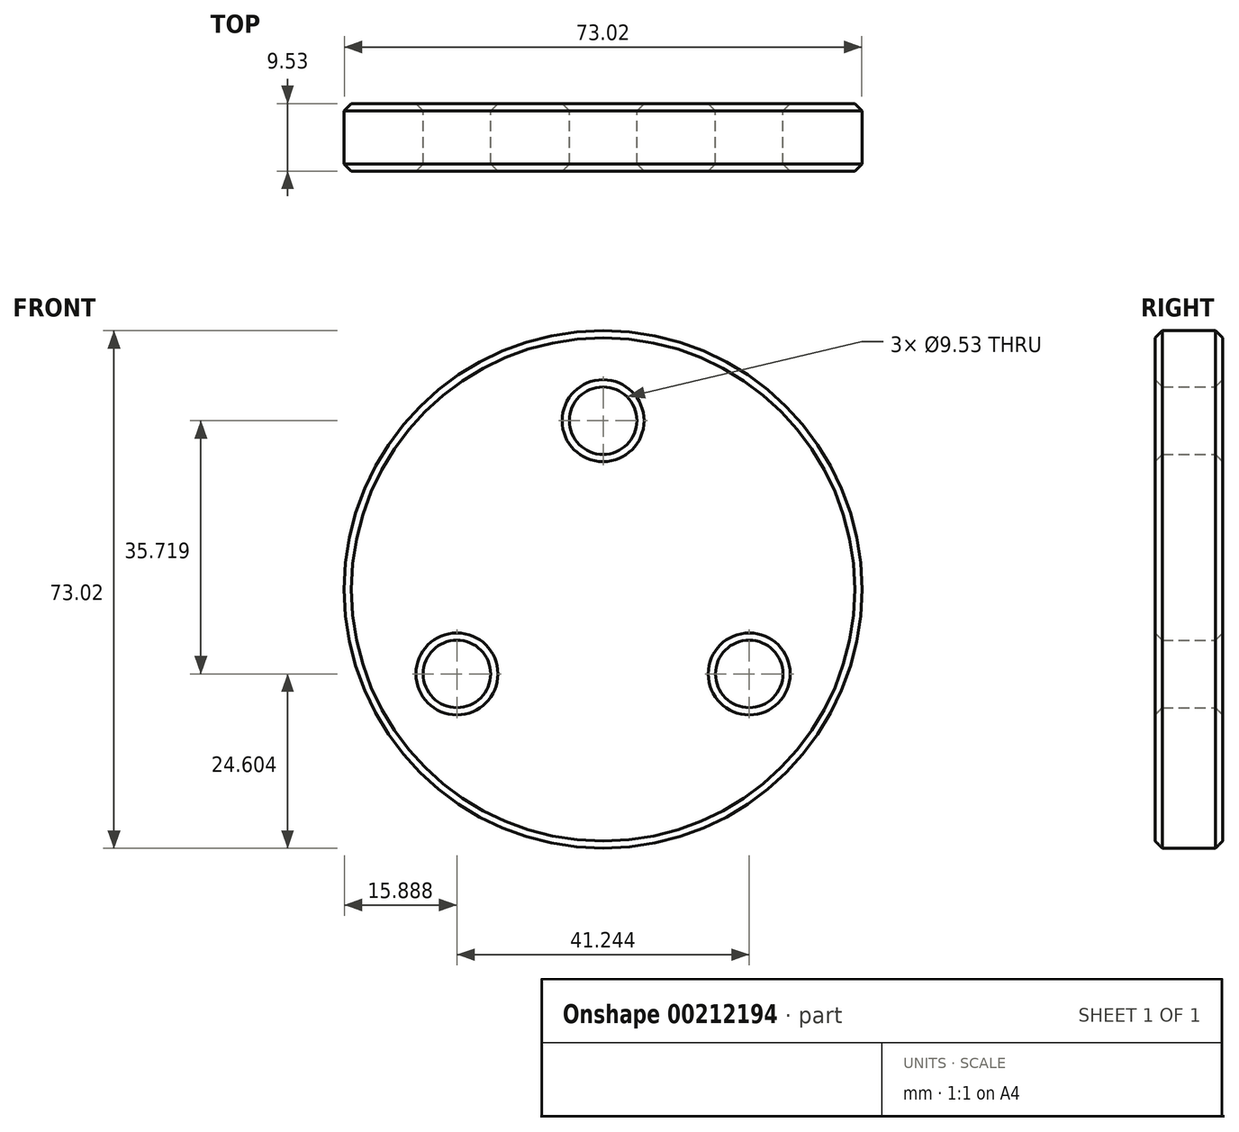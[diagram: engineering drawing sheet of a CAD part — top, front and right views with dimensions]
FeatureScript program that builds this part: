
annotation { "Feature Type Name" : "Feature", "Feature Type Description" : "" }
export const myFeature = defineFeature(function(context is Context, id is Id, definition is map)
    precondition{}
    {
        {
            var Q0;
            Q0=qCreatedBy(makeId("Front.planeOp"),FACE);
            var sketch = newSketch(context, id + "F0", { "sketchPlane" : qUnion([Q0])});
            skCircle(sketch, "E0", {"center": v(0, 0) * mm, "radius": 36.51 * mm});
            skCircle(sketch, "E1", {"center": v(0, 0) * mm, "radius": 23.81 * mm, "construction": true});
            skCircle(sketch, "E2", {"center": v(0, 23.81) * mm, "radius": 4.76 * mm});
            skCircle(sketch, "E3.1.0", {"center": v(-20.62, -11.9) * mm, "radius": 4.76 * mm});
            skCircle(sketch, "E3.2.0", {"center": v(20.62, -11.9) * mm, "radius": 4.76 * mm});
            skSolve(sketch);
        }
        {
            var Q0;
            Q0=makeQuery(id+"F0.imprint","IMPRINT",FACE,{"disambiguationData":[TD([[makeQuery(id+"F0.imprint","IMPRINT",EDGE,{"derivedFrom":sQuery(id+"F0.wireOp",EDGE,"E0")}),1.0]])]});
            extrude(context, id + "F1", {"entities" : qUnion([Q0]), "depth" : 9.52 * mm});
        }
        {
            var Q0;
            Q0=makeQuery(id+"F1.opExtrude","CAP_FACE",FACE,{"disambiguationData":[OSD([sQuery(id+"F0.wireOp",EDGE,"E0"),sQuery(id+"F0.wireOp",EDGE,"E2"),sQuery(id+"F0.wireOp",EDGE,"E3.1.0"),sQuery(id+"F0.wireOp",EDGE,"E3.2.0")])],"isStart":false});
            var Q1;
            Q1=makeQuery(id+"F1.opExtrude","CAP_FACE",FACE,{"disambiguationData":[OSD([sQuery(id+"F0.wireOp",EDGE,"E0"),sQuery(id+"F0.wireOp",EDGE,"E2"),sQuery(id+"F0.wireOp",EDGE,"E3.1.0"),sQuery(id+"F0.wireOp",EDGE,"E3.2.0")])],"isStart":true});
            chamfer(context, id + "F2", {"entities" : qUnion([Q0, Q1]), "width" : 1.02 * mm, "tangentPropagation" : true});
        }
    });
